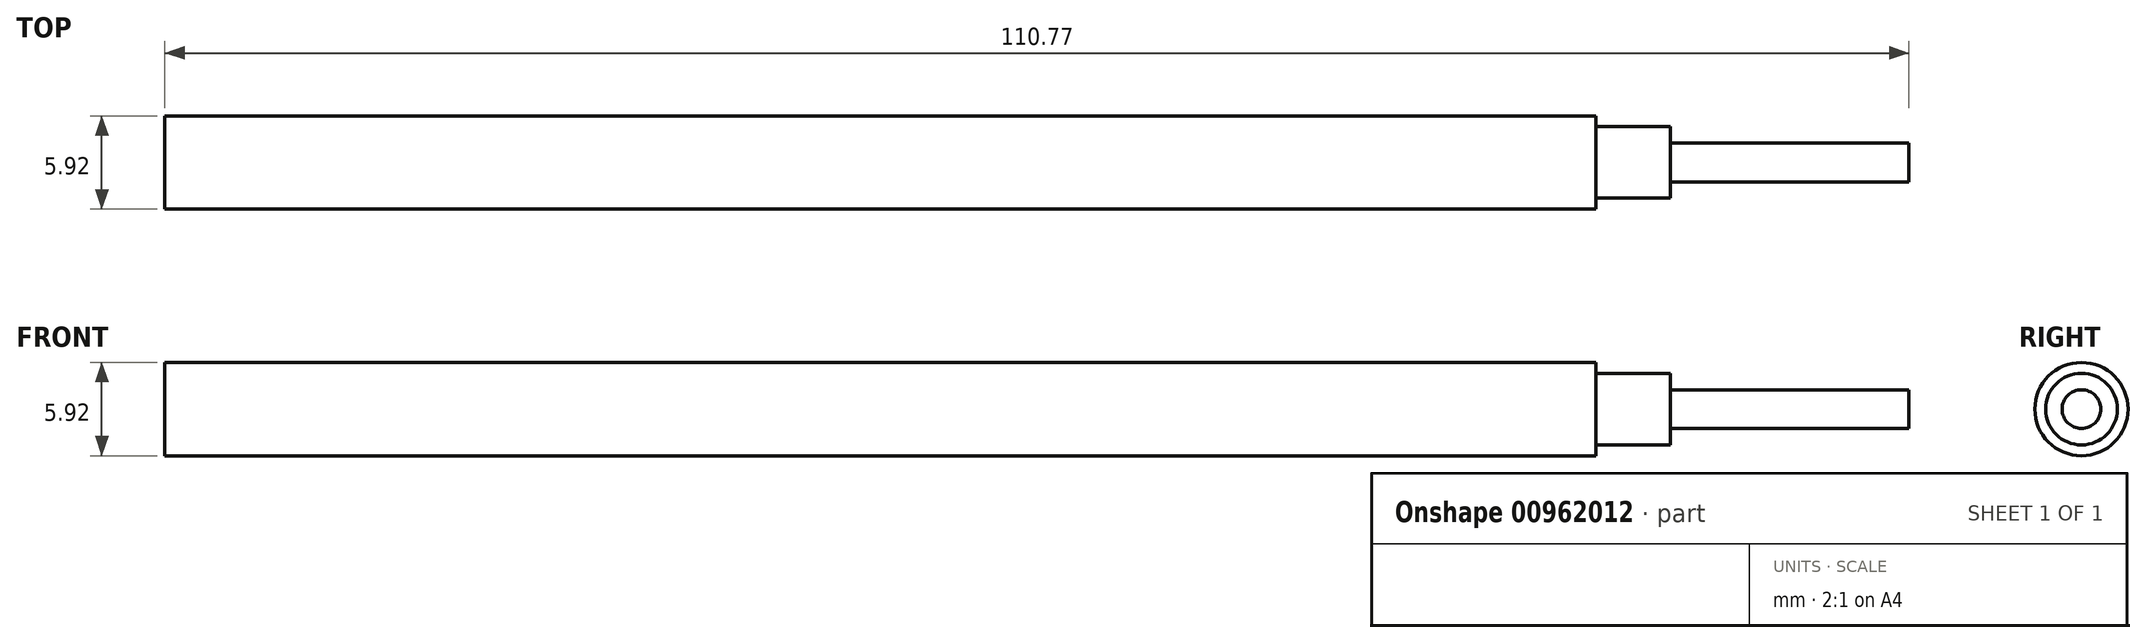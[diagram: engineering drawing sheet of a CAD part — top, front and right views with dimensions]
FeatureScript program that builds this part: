
annotation { "Feature Type Name" : "Feature", "Feature Type Description" : "" }
export const myFeature = defineFeature(function(context is Context, id is Id, definition is map)
    precondition{}
    {
        {
            var Q0;
            Q0=qCreatedBy(makeId("Front.planeOp"),FACE);
            var sketch = newSketch(context, id + "F0", { "sketchPlane" : qUnion([Q0])});
            skLineSegment(sketch, "E0", {"start": v(0, 0) * mm, "end": v(-110.77, 0) * mm});
            skLineSegment(sketch, "E1", {"start": v(-110.77, 0) * mm, "end": v(-110.77, 2.96) * mm});
            skLineSegment(sketch, "E2", {"start": v(-110.77, 2.96) * mm, "end": v(-19.89, 2.96) * mm});
            skLineSegment(sketch, "E3", {"start": v(-19.89, 2.96) * mm, "end": v(-19.89, 2.27) * mm});
            skLineSegment(sketch, "E4", {"start": v(-19.89, 2.27) * mm, "end": v(-15.16, 2.27) * mm});
            skLineSegment(sketch, "E5", {"start": v(-15.16, 2.27) * mm, "end": v(-15.16, 1.23) * mm});
            skLineSegment(sketch, "E6", {"start": v(-15.16, 1.23) * mm, "end": v(0, 1.23) * mm});
            skLineSegment(sketch, "E7", {"start": v(0, 1.23) * mm, "end": v(0, 0) * mm});
            skSolve(sketch);
        }
        {
            var Q0;
            Q0=makeQuery(id+"F0.imprint","IMPRINT",FACE,{"disambiguationData":[TD([[makeQuery(id+"F0.imprint","IMPRINT",EDGE,{"derivedFrom":sQuery(id+"F0.wireOp",EDGE,"E0")}),-1.0]])]});
            var Q1;
            Q1=sQuery(id+"F0.wireOp",EDGE,"E0");
            revolve(context, id + "F1", {"surfaceOperationType" : NewSurfaceOperationType.NEW, "entities" : qUnion([Q0]), "axis" : qUnion([Q1]), "revolveType" : RevolveType.FULL});
        }
    });
